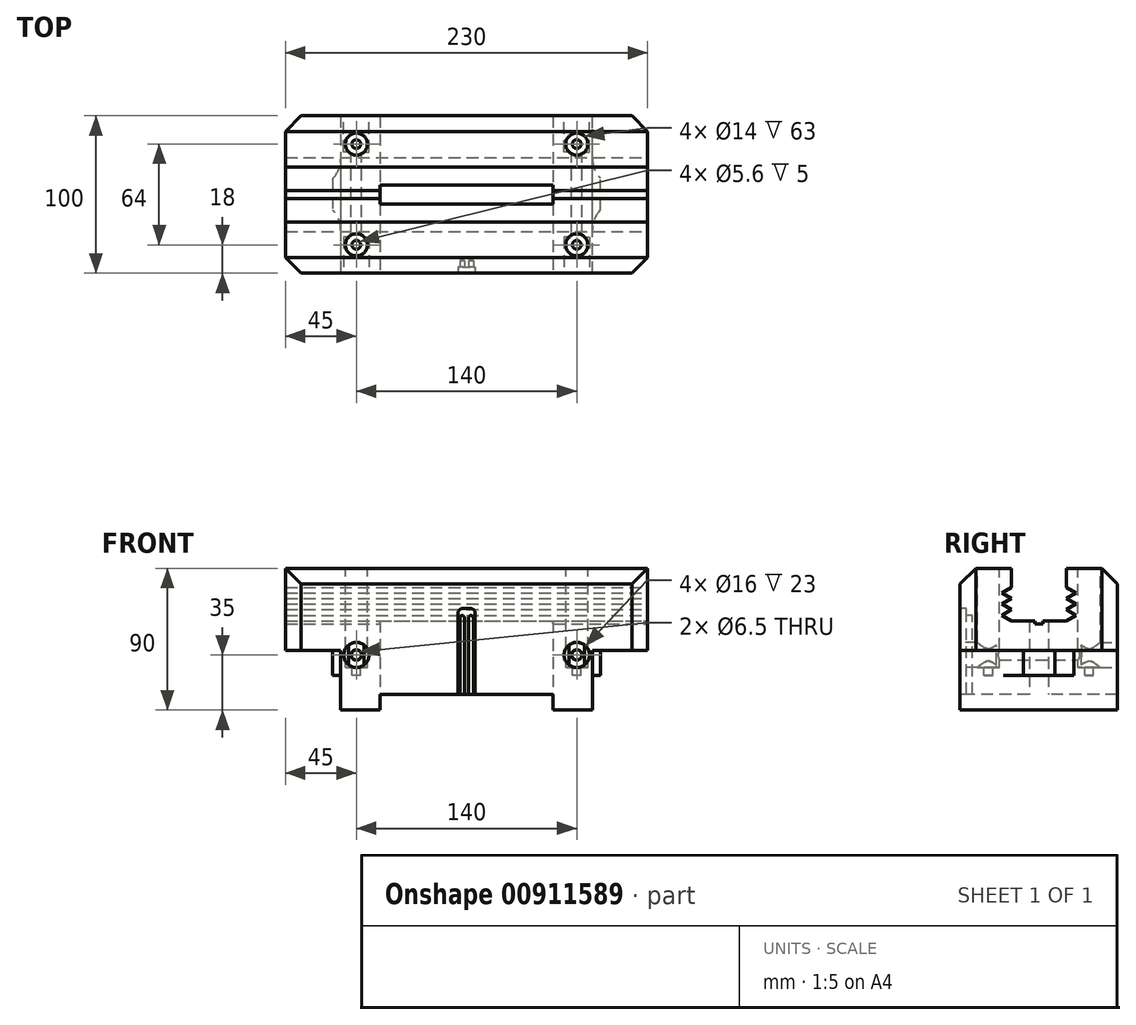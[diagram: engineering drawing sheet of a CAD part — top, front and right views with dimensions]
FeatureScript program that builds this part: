
annotation { "Feature Type Name" : "Feature", "Feature Type Description" : "" }
export const myFeature = defineFeature(function(context is Context, id is Id, definition is map)
    precondition{}
    {
        {
            var Q0;
            Q0=qCreatedBy(makeId("Top.planeOp"),FACE);
            var sketch = newSketch(context, id + "F0", { "sketchPlane" : qUnion([Q0])});
            skLineSegment(sketch, "E0.bottom", {"start": v(-115, 50) * mm, "end": v(115, 50) * mm});
            skLineSegment(sketch, "E0.top", {"start": v(-115, -50) * mm, "end": v(115, -50) * mm});
            skLineSegment(sketch, "E0.left", {"start": v(-115, 50) * mm, "end": v(-115, -50) * mm});
            skLineSegment(sketch, "E0.right", {"start": v(115, 50) * mm, "end": v(115, -50) * mm});
            skSolve(sketch);
        }
        {
            var Q0;
            Q0=makeQuery(id+"F0.imprint","IMPRINT",FACE,{"disambiguationData":[TD([[makeQuery(id+"F0.imprint","IMPRINT",EDGE,{"derivedFrom":sQuery(id+"F0.wireOp",EDGE,"E0.bottom")}),-1.0]])]});
            extrude(context, id + "F1", {"entities" : qUnion([Q0]), "oppositeDirection" : true, "depth" : 52 * mm, "offsetDistance" : 25 * mm});
        }
        {
            var Q0;
            Q0=makeQuery(id+"F1.opExtrude","SWEPT_FACE",FACE,{"disambiguationData":[OSD([sQuery(id+"F0.wireOp",EDGE,"E0.right")])]});
            var sketch = newSketch(context, id + "F2", { "sketchPlane" : qUnion([Q0])});
            skLineSegment(sketch, "E1", {"start": v(-17.5, 0) * mm, "end": v(17.5, 0) * mm});
            skLineSegment(sketch, "E2", {"start": v(-17.5, 0) * mm, "end": v(-17.5, -12) * mm});
            skLineSegment(sketch, "E3", {"start": v(-17.5, -12) * mm, "end": v(-23.52, -15.55) * mm});
            skLineSegment(sketch, "E4", {"start": v(-23.52, -15.55) * mm, "end": v(-17.5, -19.1) * mm});
            skLineSegment(sketch, "E5", {"start": v(-17.5, -19.1) * mm, "end": v(-23.52, -22.65) * mm});
            skLineSegment(sketch, "E6", {"start": v(-23.52, -22.65) * mm, "end": v(-17.5, -26.2) * mm});
            skLineSegment(sketch, "E7", {"start": v(-17.5, -26.2) * mm, "end": v(-23.52, -29.75) * mm});
            skLineSegment(sketch, "E8", {"start": v(-23.52, -29.75) * mm, "end": v(-17.5, -33.3) * mm});
            skLineSegment(sketch, "E9", {"start": v(17.5, 0) * mm, "end": v(17.5, -12) * mm});
            skLineSegment(sketch, "E10", {"start": v(17.5, -33.3) * mm, "end": v(23.52, -29.75) * mm});
            skLineSegment(sketch, "E11", {"start": v(23.52, -29.75) * mm, "end": v(17.5, -26.2) * mm});
            skLineSegment(sketch, "E12", {"start": v(17.5, -26.2) * mm, "end": v(23.52, -22.65) * mm});
            skLineSegment(sketch, "E13", {"start": v(23.52, -22.65) * mm, "end": v(17.5, -19.1) * mm});
            skLineSegment(sketch, "E14", {"start": v(17.5, -19.1) * mm, "end": v(23.52, -15.55) * mm});
            skLineSegment(sketch, "E15", {"start": v(23.52, -15.55) * mm, "end": v(17.5, -12) * mm});
            skLineSegment(sketch, "E16", {"start": v(-17.5, -33.3) * mm, "end": v(-2.5, -33.3) * mm});
            skLineSegment(sketch, "E17", {"start": v(17.5, -33.3) * mm, "end": v(2.5, -33.3) * mm});
            skLineSegment(sketch, "E18", {"start": v(-2.5, -33.3) * mm, "end": v(-2.5, -35.3) * mm});
            skLineSegment(sketch, "E19", {"start": v(2.5, -33.3) * mm, "end": v(2.5, -35.3) * mm});
            skLineSegment(sketch, "E20", {"start": v(2.5, -35.3) * mm, "end": v(-2.5, -35.3) * mm});
            skSolve(sketch);
        }
        {
            var Q0;
            Q0=makeQuery(id+"F2.imprint","IMPRINT",FACE,{"disambiguationData":[TD([[makeQuery(id+"F2.imprint","IMPRINT",EDGE,{"derivedFrom":sQuery(id+"F2.wireOp",EDGE,"E1")}),1.0]])]});
            extrude(context, id + "F3", {"entities" : qUnion([Q0]), "operationType" : NewBodyOperationType.REMOVE, "endBound" : BoundingType.UP_TO_NEXT, "oppositeDirection" : true, "depth" : 218 * mm, "offsetDistance" : 25 * mm});
        }
        {
            var Q0;
            Q0=makeQuery(id+"F1.opExtrude","CAP_EDGE",EDGE,{"disambiguationData":[OSD([sQuery(id+"F0.wireOp",EDGE,"E0.bottom")])],"isStart":true});
            var Q1;
            Q1=makeQuery(id+"F1.opExtrude","CAP_EDGE",EDGE,{"disambiguationData":[OSD([sQuery(id+"F0.wireOp",EDGE,"E0.top")])],"isStart":true});
            var Q2;
            Q2=makeQuery(id+"F1.opExtrude","SWEPT_EDGE",EDGE,{"disambiguationData":[OSD([sQuery(id+"F0.wireOp",EDGE,"E0.top"),sQuery(id+"F0.wireOp",EDGE,"E0.right")])]});
            var Q3;
            Q3=makeQuery(id+"F1.opExtrude","SWEPT_EDGE",EDGE,{"disambiguationData":[OSD([sQuery(id+"F0.wireOp",EDGE,"E0.bottom"),sQuery(id+"F0.wireOp",EDGE,"E0.right")])]});
            var Q4;
            Q4=makeQuery(id+"F1.opExtrude","SWEPT_EDGE",EDGE,{"disambiguationData":[OSD([sQuery(id+"F0.wireOp",EDGE,"E0.top"),sQuery(id+"F0.wireOp",EDGE,"E0.left")])]});
            var Q5;
            Q5=makeQuery(id+"F1.opExtrude","SWEPT_EDGE",EDGE,{"disambiguationData":[OSD([sQuery(id+"F0.wireOp",EDGE,"E0.bottom"),sQuery(id+"F0.wireOp",EDGE,"E0.left")])]});
            chamfer(context, id + "F4", {"entities" : qUnion([Q0, Q1, Q2, Q3, Q4, Q5]), "width" : 10 * mm, "tangentPropagation" : true});
        }
        {
            var Q0;
            Q0=makeQuery(id+"F1.opExtrude","CAP_FACE",FACE,{"disambiguationData":[OSD([sQuery(id+"F0.wireOp",EDGE,"E0.bottom"),sQuery(id+"F0.wireOp",EDGE,"E0.top"),sQuery(id+"F0.wireOp",EDGE,"E0.left"),sQuery(id+"F0.wireOp",EDGE,"E0.right")])],"isStart":false});
            var sketch = newSketch(context, id + "F5", { "sketchPlane" : qUnion([Q0])});
            skLineSegment(sketch, "E21", {"start": v(80, 50) * mm, "end": v(80, -50) * mm});
            skLineSegment(sketch, "E22", {"start": v(80, -50) * mm, "end": v(-80, -50) * mm});
            skLineSegment(sketch, "E23", {"start": v(-80, -50) * mm, "end": v(-80, 50) * mm});
            skLineSegment(sketch, "E24", {"start": v(-80, 50) * mm, "end": v(80, 50) * mm});
            skSolve(sketch);
        }
        {
            var Q0;
            Q0=makeQuery(id+"F5.imprint","IMPRINT",FACE,{"disambiguationData":[TD([[makeQuery(id+"F5.imprint","IMPRINT",EDGE,{"derivedFrom":sQuery(id+"F5.wireOp",EDGE,"E21")}),-1.0]])]});
            extrude(context, id + "F6", {"entities" : qUnion([Q0]), "operationType" : NewBodyOperationType.ADD, "depth" : 38 * mm, "offsetDistance" : 25 * mm});
        }
        {
            var Q0;
            {var subQ0=sQuery(id+"F0.wireOp",EDGE,"E0.bottom");var subQ1=sQuery(id+"F0.wireOp",EDGE,"E0.right");var subQ2=sQuery(id+"F0.wireOp",EDGE,"E0.left");Q0=makeQuery(id+"F3.boolean.opBoolean","SPLIT",FACE,{"disambiguationData":[TD([makeQuery(id+"F1.opExtrude","SWEPT_FACE",FACE,{"disambiguationData":[OSD([subQ0])]})])],"derivedFrom":makeQuery(id+"F1.opExtrude","CAP_FACE",FACE,{"disambiguationData":[OSD([subQ0,sQuery(id+"F0.wireOp",EDGE,"E0.top"),subQ2,subQ1])],"isStart":true})});}
            var sketch = newSketch(context, id + "F7", { "sketchPlane" : qUnion([Q0])});
            skCircle(sketch, "E25", {"center": v(70, -32) * mm, "radius": 7 * mm});
            skCircle(sketch, "E26", {"center": v(-70, -32) * mm, "radius": 7 * mm});
            skCircle(sketch, "E27", {"center": v(-70, 32) * mm, "radius": 7 * mm});
            skCircle(sketch, "E28", {"center": v(70, 32) * mm, "radius": 7 * mm});
            skCircle(sketch, "E29", {"center": v(-70, 32) * mm, "radius": 2.8 * mm});
            skCircle(sketch, "E30", {"center": v(70, 32) * mm, "radius": 2.8 * mm});
            skCircle(sketch, "E31", {"center": v(70, -32) * mm, "radius": 2.8 * mm});
            skCircle(sketch, "E32", {"center": v(-70, -32) * mm, "radius": 2.8 * mm});
            skSolve(sketch);
        }
        {
            var Q0;
            Q0=qSketchRegion(id+"F7",true);
            extrude(context, id + "F8", {"entities" : qUnion([Q0]), "operationType" : NewBodyOperationType.REMOVE, "oppositeDirection" : true, "depth" : 63 * mm, "offsetDistance" : 25 * mm});
        }
        {
            var Q0;
            {var subQ0=sQuery(id+"F0.wireOp",EDGE,"E0.bottom");var subQ1=sQuery(id+"F0.wireOp",EDGE,"E0.right");var subQ2=sQuery(id+"F0.wireOp",EDGE,"E0.left");Q0=makeQuery(id+"F8.boolean.opBoolean","SPLIT",FACE,{"disambiguationData":[TD([makeQuery(id+"F8.opExtrude","SWEPT_FACE",FACE,{"disambiguationData":[OSD([sQuery(id+"F7.wireOp",EDGE,"E30")])]})])],"derivedFrom":makeQuery(id+"F3.boolean.opBoolean","SPLIT",FACE,{"disambiguationData":[TD([makeQuery(id+"F1.opExtrude","SWEPT_FACE",FACE,{"disambiguationData":[OSD([subQ0])]})])],"derivedFrom":makeQuery(id+"F1.opExtrude","CAP_FACE",FACE,{"disambiguationData":[OSD([subQ0,sQuery(id+"F0.wireOp",EDGE,"E0.top"),subQ2,subQ1])],"isStart":true})})});}
            var Q1;
            {var subQ0=sQuery(id+"F0.wireOp",EDGE,"E0.bottom");var subQ1=sQuery(id+"F0.wireOp",EDGE,"E0.right");var subQ2=sQuery(id+"F0.wireOp",EDGE,"E0.left");Q1=makeQuery(id+"F8.boolean.opBoolean","SPLIT",FACE,{"disambiguationData":[TD([makeQuery(id+"F8.opExtrude","SWEPT_FACE",FACE,{"disambiguationData":[OSD([sQuery(id+"F7.wireOp",EDGE,"E29")])]})])],"derivedFrom":makeQuery(id+"F3.boolean.opBoolean","SPLIT",FACE,{"disambiguationData":[TD([makeQuery(id+"F1.opExtrude","SWEPT_FACE",FACE,{"disambiguationData":[OSD([subQ0])]})])],"derivedFrom":makeQuery(id+"F1.opExtrude","CAP_FACE",FACE,{"disambiguationData":[OSD([subQ0,sQuery(id+"F0.wireOp",EDGE,"E0.top"),subQ2,subQ1])],"isStart":true})})});}
            var Q2;
            {var subQ0=sQuery(id+"F0.wireOp",EDGE,"E0.top");var subQ1=sQuery(id+"F0.wireOp",EDGE,"E0.left");var subQ2=sQuery(id+"F0.wireOp",EDGE,"E0.right");Q2=makeQuery(id+"F8.boolean.opBoolean","SPLIT",FACE,{"disambiguationData":[TD([makeQuery(id+"F8.opExtrude","SWEPT_FACE",FACE,{"disambiguationData":[OSD([sQuery(id+"F7.wireOp",EDGE,"E32")])]})])],"derivedFrom":makeQuery(id+"F3.boolean.opBoolean","SPLIT",FACE,{"disambiguationData":[TD([makeQuery(id+"F1.opExtrude","SWEPT_FACE",FACE,{"disambiguationData":[OSD([subQ0])]})])],"derivedFrom":makeQuery(id+"F1.opExtrude","CAP_FACE",FACE,{"disambiguationData":[OSD([sQuery(id+"F0.wireOp",EDGE,"E0.bottom"),subQ0,subQ1,subQ2])],"isStart":true})})});}
            var Q3;
            {var subQ0=sQuery(id+"F0.wireOp",EDGE,"E0.top");var subQ1=sQuery(id+"F0.wireOp",EDGE,"E0.left");var subQ2=sQuery(id+"F0.wireOp",EDGE,"E0.right");Q3=makeQuery(id+"F8.boolean.opBoolean","SPLIT",FACE,{"disambiguationData":[TD([makeQuery(id+"F8.opExtrude","SWEPT_FACE",FACE,{"disambiguationData":[OSD([sQuery(id+"F7.wireOp",EDGE,"E31")])]})])],"derivedFrom":makeQuery(id+"F3.boolean.opBoolean","SPLIT",FACE,{"disambiguationData":[TD([makeQuery(id+"F1.opExtrude","SWEPT_FACE",FACE,{"disambiguationData":[OSD([subQ0])]})])],"derivedFrom":makeQuery(id+"F1.opExtrude","CAP_FACE",FACE,{"disambiguationData":[OSD([sQuery(id+"F0.wireOp",EDGE,"E0.bottom"),subQ0,subQ1,subQ2])],"isStart":true})})});}
            extrude(context, id + "F9", {"entities" : qUnion([Q0, Q1, Q2, Q3]), "operationType" : NewBodyOperationType.REMOVE, "oppositeDirection" : true, "depth" : 68 * mm, "offsetDistance" : 25 * mm});
        }
        {
            var Q0;
            Q0=makeQuery(id+"F6.boolean.opBoolean","MERGE",FACE,{"derivedFrom":[makeQuery(id+"F1.opExtrude","SWEPT_FACE",FACE,{"disambiguationData":[OSD([sQuery(id+"F0.wireOp",EDGE,"E0.bottom")])]}),makeQuery(id+"F6.opExtrude","SWEPT_FACE",FACE,{"disambiguationData":[OSD([sQuery(id+"F5.wireOp",EDGE,"E22")])]})]});
            var sketch = newSketch(context, id + "F10", { "sketchPlane" : qUnion([Q0])});
            skCircle(sketch, "E33", {"center": v(70, -55) * mm, "radius": 8 * mm});
            skCircle(sketch, "E34", {"center": v(-70, -55) * mm, "radius": 8 * mm});
            skCircle(sketch, "E35", {"center": v(70, -55) * mm, "radius": 3.25 * mm});
            skCircle(sketch, "E36", {"center": v(-70, -55) * mm, "radius": 3.25 * mm});
            skSolve(sketch);
        }
        {
            var Q0;
            Q0=qSketchRegion(id+"F10",true);
            extrude(context, id + "F11", {"entities" : qUnion([Q0]), "operationType" : NewBodyOperationType.REMOVE, "oppositeDirection" : true, "depth" : 23 * mm, "offsetDistance" : 25 * mm});
        }
        {
            var Q0;
            Q0=makeQuery(id+"F11.boolean.opBoolean","SPLIT",FACE,{"disambiguationData":[TD([makeQuery(id+"F11.opExtrude","SWEPT_FACE",FACE,{"disambiguationData":[OSD([sQuery(id+"F10.wireOp",EDGE,"E36")])]})])],"derivedFrom":makeQuery(id+"F6.boolean.opBoolean","MERGE",FACE,{"derivedFrom":[makeQuery(id+"F1.opExtrude","SWEPT_FACE",FACE,{"disambiguationData":[OSD([sQuery(id+"F0.wireOp",EDGE,"E0.bottom")])]}),makeQuery(id+"F6.opExtrude","SWEPT_FACE",FACE,{"disambiguationData":[OSD([sQuery(id+"F5.wireOp",EDGE,"E22")])]})]})});
            var Q1;
            Q1=makeQuery(id+"F11.boolean.opBoolean","SPLIT",FACE,{"disambiguationData":[TD([makeQuery(id+"F11.opExtrude","SWEPT_FACE",FACE,{"disambiguationData":[OSD([sQuery(id+"F10.wireOp",EDGE,"E35")])]})])],"derivedFrom":makeQuery(id+"F6.boolean.opBoolean","MERGE",FACE,{"derivedFrom":[makeQuery(id+"F1.opExtrude","SWEPT_FACE",FACE,{"disambiguationData":[OSD([sQuery(id+"F0.wireOp",EDGE,"E0.bottom")])]}),makeQuery(id+"F6.opExtrude","SWEPT_FACE",FACE,{"disambiguationData":[OSD([sQuery(id+"F5.wireOp",EDGE,"E22")])]})]})});
            extrude(context, id + "F12", {"entities" : qUnion([Q0, Q1]), "operationType" : NewBodyOperationType.REMOVE, "oppositeDirection" : true, "depth" : 179.1 * mm, "offsetDistance" : 25 * mm});
        }
        {
            var Q0;
            Q0=makeQuery(id+"F6.boolean.opBoolean","MERGE",FACE,{"derivedFrom":[makeQuery(id+"F1.opExtrude","SWEPT_FACE",FACE,{"disambiguationData":[OSD([sQuery(id+"F0.wireOp",EDGE,"E0.top")])]}),makeQuery(id+"F6.opExtrude","SWEPT_FACE",FACE,{"disambiguationData":[OSD([sQuery(id+"F5.wireOp",EDGE,"E24")])]})]});
            var sketch = newSketch(context, id + "F13", { "sketchPlane" : qUnion([Q0])});
            skCircle(sketch, "E37", {"center": v(-70, -55) * mm, "radius": 8 * mm});
            skCircle(sketch, "E38", {"center": v(-70, -55) * mm, "radius": 3.25 * mm});
            skCircle(sketch, "E39", {"center": v(70, -55) * mm, "radius": 8 * mm});
            skCircle(sketch, "E40", {"center": v(70, -55) * mm, "radius": 3.25 * mm});
            skLineSegment(sketch, "E41.bottom", {"start": v(-55, -90) * mm, "end": v(55, -90) * mm});
            skLineSegment(sketch, "E41.top", {"start": v(-55, -80) * mm, "end": v(55, -80) * mm});
            skLineSegment(sketch, "E41.left", {"start": v(-55, -90) * mm, "end": v(-55, -80) * mm});
            skLineSegment(sketch, "E41.right", {"start": v(55, -90) * mm, "end": v(55, -80) * mm});
            skSolve(sketch);
        }
        {
            var Q0;
            Q0=qSketchRegion(id+"F13",true);
            extrude(context, id + "F14", {"entities" : qUnion([Q0]), "operationType" : NewBodyOperationType.REMOVE, "oppositeDirection" : true, "depth" : 23 * mm, "offsetDistance" : 25 * mm});
        }
        {
            var Q0;
            Q0=makeQuery(id+"F13.imprint","IMPRINT",FACE,{"disambiguationData":[TD([[makeQuery(id+"F13.imprint","IMPRINT",EDGE,{"derivedFrom":sQuery(id+"F13.wireOp",EDGE,"E41.bottom")}),1.0]])]});
            extrude(context, id + "F15", {"entities" : qUnion([Q0]), "operationType" : NewBodyOperationType.REMOVE, "endBound" : BoundingType.THROUGH_ALL, "oppositeDirection" : true, "depth" : 25 * mm, "offsetDistance" : 25 * mm});
        }
        {
            var Q0;
            Q0=makeQuery(id+"F6.opExtrude","SWEPT_FACE",FACE,{"disambiguationData":[OSD([sQuery(id+"F5.wireOp",EDGE,"E23")])]});
            var sketch = newSketch(context, id + "F16", { "sketchPlane" : qUnion([Q0])});
            skLineSegment(sketch, "E42.bottom", {"start": v(-22.5, -52) * mm, "end": v(22.5, -52) * mm});
            skLineSegment(sketch, "E42.top", {"start": v(-22.5, -68) * mm, "end": v(22.5, -68) * mm});
            skLineSegment(sketch, "E42.left", {"start": v(-22.5, -52) * mm, "end": v(-22.5, -68) * mm});
            skLineSegment(sketch, "E42.right", {"start": v(22.5, -52) * mm, "end": v(22.5, -68) * mm});
            skSolve(sketch);
        }
        {
            var Q0;
            Q0=makeQuery(id+"F16.imprint","IMPRINT",FACE,{"disambiguationData":[TD([[makeQuery(id+"F16.imprint","IMPRINT",EDGE,{"derivedFrom":sQuery(id+"F16.wireOp",EDGE,"E42.bottom")}),-1.0]])]});
            extrude(context, id + "F17", {"entities" : qUnion([Q0]), "operationType" : NewBodyOperationType.ADD, "depth" : 5 * mm, "offsetDistance" : 25 * mm});
        }
        {
            var Q0;
            Q0=makeQuery(id+"F17.opExtrude","SWEPT_FACE",FACE,{"disambiguationData":[OSD([sQuery(id+"F16.wireOp",EDGE,"E42.top")])]});
            var sketch = newSketch(context, id + "F18", { "sketchPlane" : qUnion([Q0])});
            skLineSegment(sketch, "E43", {"start": v(-85, 10) * mm, "end": v(-85, -10) * mm});
            skArc(sketch, "E44", {"start": v(-80, -22.5) * mm, "mid": v(-81.3, -15.77) * mm, "end": v(-85, -10) * mm});
            skArc(sketch, "E45", {"start": v(-85, 10) * mm, "mid": v(-81.3, 15.77) * mm, "end": v(-80, 22.5) * mm});
            skSolve(sketch);
        }
        {
            var Q0;
            Q0=qSketchRegion(id+"F18",true);
            var Q1;
            {var subQ0=sQuery(id+"F18.wireOp",EDGE,"E44");Q1=makeQuery(id+"F18.imprint","IMPRINT",FACE,{"disambiguationData":[TD([[makeQuery(id+"F18.imprint","IMPRINT",EDGE,{"derivedFrom":subQ0}),1.0]])]});}
            var Q2;
            {var subQ0=sQuery(id+"F18.wireOp",EDGE,"E45");Q2=makeQuery(id+"F18.imprint","IMPRINT",FACE,{"disambiguationData":[TD([[makeQuery(id+"F18.imprint","IMPRINT",EDGE,{"derivedFrom":subQ0}),1.0]])]});}
            extrude(context, id + "F19", {"entities" : qUnion([Q0, Q1, Q2]), "operationType" : NewBodyOperationType.REMOVE, "oppositeDirection" : true, "depth" : 16 * mm, "offsetDistance" : 25 * mm});
        }
        {
            var Q0;
            Q0=makeQuery(id+"F6.opExtrude","SWEPT_FACE",FACE,{"disambiguationData":[OSD([sQuery(id+"F5.wireOp",EDGE,"E21")])]});
            var sketch = newSketch(context, id + "F20", { "sketchPlane" : qUnion([Q0])});
            skLineSegment(sketch, "E46.bottom", {"start": v(-22.5, -52) * mm, "end": v(22.5, -52) * mm});
            skLineSegment(sketch, "E46.top", {"start": v(-22.5, -68) * mm, "end": v(22.5, -68) * mm});
            skLineSegment(sketch, "E46.left", {"start": v(-22.5, -52) * mm, "end": v(-22.5, -68) * mm});
            skLineSegment(sketch, "E46.right", {"start": v(22.5, -52) * mm, "end": v(22.5, -68) * mm});
            skSolve(sketch);
        }
        {
            var Q0;
            Q0=makeQuery(id+"F20.imprint","IMPRINT",FACE,{"disambiguationData":[TD([[makeQuery(id+"F20.imprint","IMPRINT",EDGE,{"derivedFrom":sQuery(id+"F20.wireOp",EDGE,"E46.bottom")}),-1.0]])]});
            extrude(context, id + "F21", {"entities" : qUnion([Q0]), "operationType" : NewBodyOperationType.ADD, "depth" : 5 * mm, "offsetDistance" : 25 * mm});
        }
        {
            var Q0;
            Q0=makeQuery(id+"F21.opExtrude","SWEPT_FACE",FACE,{"disambiguationData":[OSD([sQuery(id+"F20.wireOp",EDGE,"E46.top")])]});
            var sketch = newSketch(context, id + "F22", { "sketchPlane" : qUnion([Q0])});
            skLineSegment(sketch, "E47", {"start": v(85, -10.3) * mm, "end": v(85, 9.7) * mm});
            skArc(sketch, "E48", {"start": v(80, 22.5) * mm, "mid": v(81.3, 15.63) * mm, "end": v(85, 9.7) * mm});
            skArc(sketch, "E49", {"start": v(85, -10.3) * mm, "mid": v(81.35, -15.93) * mm, "end": v(80, -22.5) * mm});
            skSolve(sketch);
        }
        {
            var Q0;
            Q0=qSketchRegion(id+"F22",true);
            var Q1;
            {var subQ0=sQuery(id+"F22.wireOp",EDGE,"E49");Q1=makeQuery(id+"F22.imprint","IMPRINT",FACE,{"disambiguationData":[TD([[makeQuery(id+"F22.imprint","IMPRINT",EDGE,{"derivedFrom":subQ0}),1.0]])]});}
            var Q2;
            {var subQ0=sQuery(id+"F22.wireOp",EDGE,"E48");Q2=makeQuery(id+"F22.imprint","IMPRINT",FACE,{"disambiguationData":[TD([[makeQuery(id+"F22.imprint","IMPRINT",EDGE,{"derivedFrom":subQ0}),1.0]])]});}
            extrude(context, id + "F23", {"entities" : qUnion([Q0, Q1, Q2]), "operationType" : NewBodyOperationType.REMOVE, "oppositeDirection" : true, "depth" : 16 * mm, "offsetDistance" : 25 * mm});
        }
        {
            var Q0;
            Q0=makeQuery(id+"F6.boolean.opBoolean","MERGE",FACE,{"derivedFrom":[makeQuery(id+"F1.opExtrude","SWEPT_FACE",FACE,{"disambiguationData":[OSD([sQuery(id+"F0.wireOp",EDGE,"E0.top")])]}),makeQuery(id+"F6.opExtrude","SWEPT_FACE",FACE,{"disambiguationData":[OSD([sQuery(id+"F5.wireOp",EDGE,"E24")])]})]});
            var sketch = newSketch(context, id + "F24", { "sketchPlane" : qUnion([Q0])});
            skLineSegment(sketch, "E50.bottom", {"start": v(-5.5, -80) * mm, "end": v(5.5, -80) * mm});
            skLineSegment(sketch, "E50.left", {"start": v(-5.5, -80) * mm, "end": v(-5.5, -31) * mm});
            skLineSegment(sketch, "E50.right", {"start": v(5.5, -80) * mm, "end": v(5.5, -31) * mm});
            skLineSegment(sketch, "E51.top", {"start": v(-2.5, -25.5) * mm, "end": v(2.5, -25.5) * mm});
            skLineSegment(sketch, "E51.left", {"start": v(-5.5, -31) * mm, "end": v(-5.5, -28.5) * mm});
            skLineSegment(sketch, "E51.right", {"start": v(5.5, -31) * mm, "end": v(5.5, -28.5) * mm});
            skPoint(sketch, "E52.visualSharp", {"position": v(5.5, -25.5) * mm});
            skArc(sketch, "E52.filletArc", {"start": v(5.5, -28.5) * mm, "mid": v(4.62, -26.38) * mm, "end": v(2.5, -25.5) * mm});
            skPoint(sketch, "E53.visualSharp", {"position": v(-5.5, -25.5) * mm});
            skArc(sketch, "E53.filletArc", {"start": v(-2.5, -25.5) * mm, "mid": v(-4.62, -26.38) * mm, "end": v(-5.5, -28.5) * mm});
            skSolve(sketch);
        }
        {
            var Q0;
            Q0=makeQuery(id+"F24.imprint","IMPRINT",FACE,{"disambiguationData":[TD([[makeQuery(id+"F24.imprint","IMPRINT",EDGE,{"derivedFrom":sQuery(id+"F24.wireOp",EDGE,"E50.bottom")}),1.0]])]});
            extrude(context, id + "F25", {"entities" : qUnion([Q0]), "operationType" : NewBodyOperationType.REMOVE, "oppositeDirection" : true, "depth" : 4 * mm, "offsetDistance" : 25 * mm});
        }
        {
            var Q0;
            Q0=makeQuery(id+"F25.boolean.opBoolean","COPY",FACE,{"derivedFrom":makeQuery(id+"F25.opExtrude","CAP_FACE",FACE,{"disambiguationData":[OSD([sQuery(id+"F24.wireOp",EDGE,"E50.bottom"),sQuery(id+"F24.wireOp",EDGE,"E50.left"),sQuery(id+"F24.wireOp",EDGE,"E50.right"),sQuery(id+"F24.wireOp",EDGE,"E51.top"),sQuery(id+"F24.wireOp",EDGE,"E51.left"),sQuery(id+"F24.wireOp",EDGE,"E51.right"),sQuery(id+"F24.wireOp",EDGE,"E52.filletArc"),sQuery(id+"F24.wireOp",EDGE,"E53.filletArc")])],"isStart":false})});
            var sketch = newSketch(context, id + "F26", { "sketchPlane" : qUnion([Q0])});
            skLineSegment(sketch, "E54.bottom", {"start": v(1.3, -80) * mm, "end": v(4.3, -80) * mm});
            skLineSegment(sketch, "E54.left", {"start": v(1.3, -80) * mm, "end": v(1.3, -31.5) * mm});
            skLineSegment(sketch, "E54.right", {"start": v(4.3, -80) * mm, "end": v(4.3, -31.5) * mm});
            skLineSegment(sketch, "E55.bottom", {"start": v(-4.3, -80) * mm, "end": v(-1.3, -80) * mm});
            skLineSegment(sketch, "E55.left", {"start": v(-4.3, -80) * mm, "end": v(-4.3, -31.5) * mm});
            skLineSegment(sketch, "E55.right", {"start": v(-1.3, -80) * mm, "end": v(-1.3, -31.5) * mm});
            skArc(sketch, "E56", {"start": v(4.3, -31.5) * mm, "mid": v(2.8, -30) * mm, "end": v(1.3, -31.5) * mm});
            skArc(sketch, "E57", {"start": v(-1.3, -31.5) * mm, "mid": v(-2.8, -30) * mm, "end": v(-4.3, -31.5) * mm});
            skSolve(sketch);
        }
        {
            var Q0;
            Q0=qSketchRegion(id+"F26",true);
            extrude(context, id + "F27", {"entities" : qUnion([Q0]), "operationType" : NewBodyOperationType.REMOVE, "oppositeDirection" : true, "depth" : 4 * mm, "offsetDistance" : 25 * mm});
        }
        {
            var Q0;
            {var subQ0=sQuery(id+"F13.wireOp",EDGE,"E41.top");Q0=makeQuery(id+"F15.boolean.opBoolean","MERGE",FACE,{"derivedFrom":[makeQuery(id+"F14.boolean.opBoolean","COPY",FACE,{"derivedFrom":makeQuery(id+"F14.opExtrude","SWEPT_FACE",FACE,{"disambiguationData":[OSD([subQ0])]})})],"fromTools":[makeQuery(id+"F15.opExtrude","SWEPT_FACE",FACE,{"disambiguationData":[OSD([subQ0])]})]});}
            var sketch = newSketch(context, id + "F28", { "sketchPlane" : qUnion([Q0])});
            skLineSegment(sketch, "E58.bottom", {"start": v(-55, 6) * mm, "end": v(55, 6) * mm});
            skLineSegment(sketch, "E58.top", {"start": v(-55, -6) * mm, "end": v(55, -6) * mm});
            skLineSegment(sketch, "E58.left", {"start": v(-55, 6) * mm, "end": v(-55, -6) * mm});
            skLineSegment(sketch, "E58.right", {"start": v(55, 6) * mm, "end": v(55, -6) * mm});
            skSolve(sketch);
        }
        {
            var Q0;
            Q0=makeQuery(id+"F28.imprint","IMPRINT",FACE,{"disambiguationData":[TD([[makeQuery(id+"F28.imprint","IMPRINT",EDGE,{"derivedFrom":sQuery(id+"F28.wireOp",EDGE,"E58.bottom")}),-1.0]])]});
            extrude(context, id + "F29", {"entities" : qUnion([Q0]), "operationType" : NewBodyOperationType.REMOVE, "oppositeDirection" : true, "depth" : 81.3 * mm, "offsetDistance" : 25 * mm});
        }
    });
